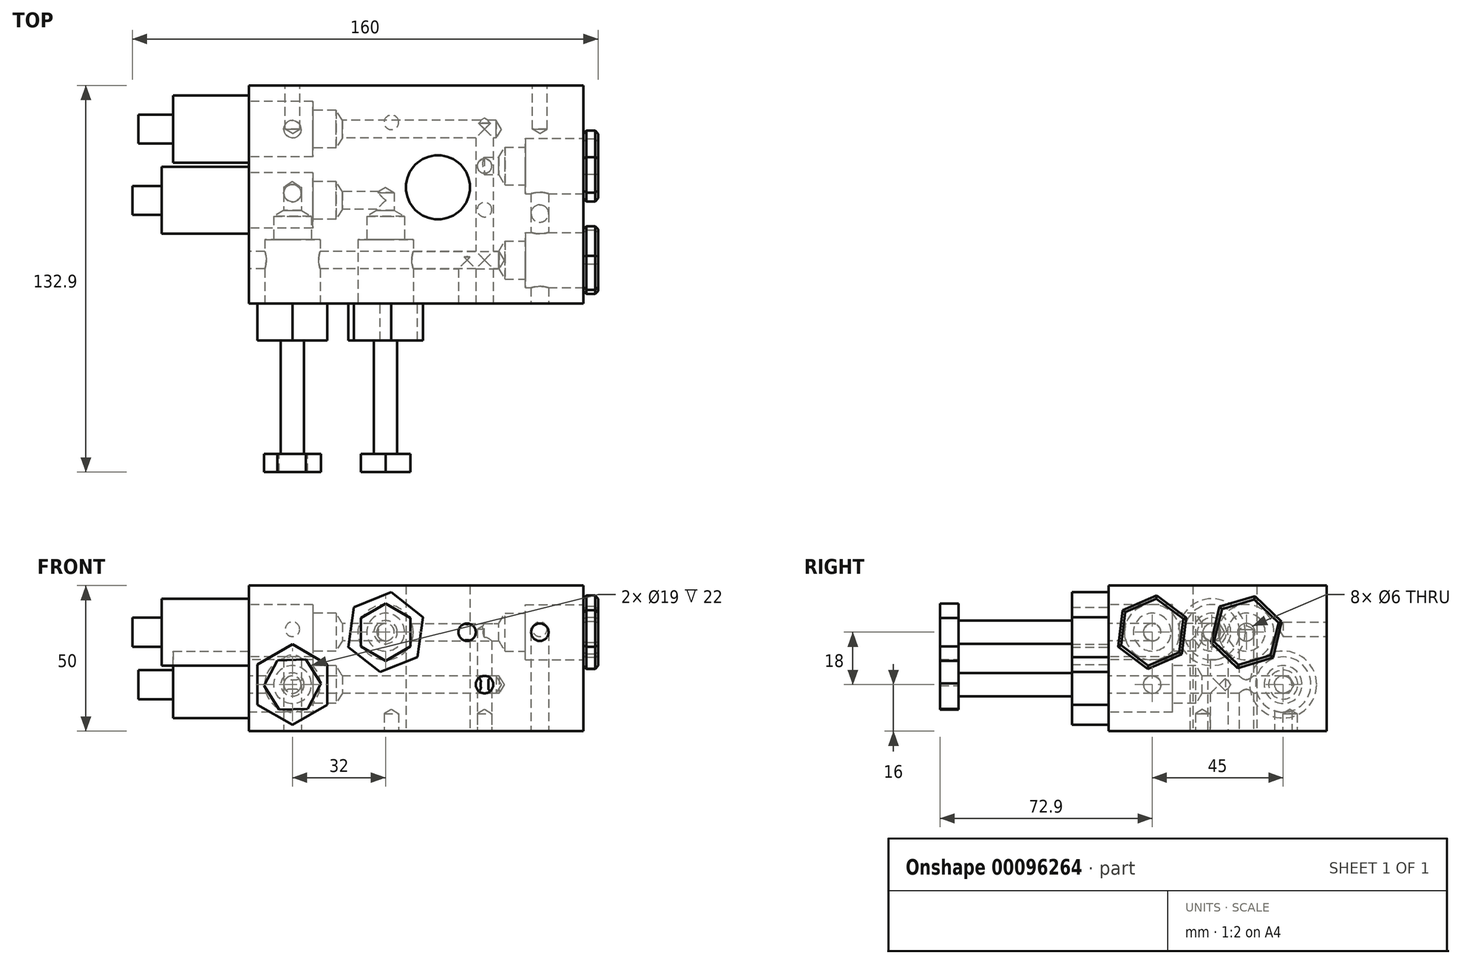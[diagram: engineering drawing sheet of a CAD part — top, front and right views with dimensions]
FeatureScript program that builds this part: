
annotation { "Feature Type Name" : "Feature", "Feature Type Description" : "" }
export const myFeature = defineFeature(function(context is Context, id is Id, definition is map)
    precondition{}
    {
        {
            var Q0;
            Q0=qCreatedBy(makeId("Top.planeOp"),FACE);
            var sketch = newSketch(context, id + "F0", { "sketchPlane" : qUnion([Q0])});
            skLineSegment(sketch, "E0.rect.bottom", {"start": v(50, 35) * mm, "end": v(-65, 35) * mm});
            skLineSegment(sketch, "E0.rect.top", {"start": v(50, -40) * mm, "end": v(-65, -40) * mm});
            skLineSegment(sketch, "E0.rect.left", {"start": v(50, 35) * mm, "end": v(50, -40) * mm});
            skLineSegment(sketch, "E0.rect.right", {"start": v(-65, 35) * mm, "end": v(-65, -40) * mm});
            skPoint(sketch, "E0.rect.middle", {"position": v(0, 0) * mm});
            skSolve(sketch);
        }
        {
            var Q0;
            Q0=makeQuery(id+"F0.imprint","IMPRINT",FACE,{"disambiguationData":[TD([[makeQuery(id+"F0.imprint","IMPRINT",EDGE,{"derivedFrom":sQuery(id+"F0.wireOp",EDGE,"E0.rect.bottom")}),1.0]])]});
            var Q1;
            Q1=makeQuery(id+"F0.imprint","IMPRINT",FACE,{"disambiguationData":[TD([[makeQuery(id+"F0.imprint","IMPRINT",EDGE,{"derivedFrom":sQuery(id+"F0.wireOp",EDGE,"7588558b-6d4b-4371-8287-17bf13519ebf.1.0.0")}),1.0]])]});
            var Q2;
            Q2=makeQuery(id+"F0.imprint","IMPRINT",FACE,{"disambiguationData":[TD([[makeQuery(id+"F0.imprint","IMPRINT",EDGE,{"derivedFrom":sQuery(id+"F0.wireOp",EDGE,"7588558b-6d4b-4371-8287-17bf13519ebf.1.1.0")}),1.0]])]});
            var Q3;
            Q3=makeQuery(id+"F0.imprint","IMPRINT",FACE,{"disambiguationData":[TD([[makeQuery(id+"F0.imprint","IMPRINT",EDGE,{"derivedFrom":sQuery(id+"F0.wireOp",EDGE,"f2f94a69-6f03-48d5-8e05-4ef8c2e551b9")}),1.0]])]});
            var Q4;
            Q4=makeQuery(id+"F0.imprint","IMPRINT",FACE,{"disambiguationData":[TD([[makeQuery(id+"F0.imprint","IMPRINT",EDGE,{"derivedFrom":sQuery(id+"F0.wireOp",EDGE,"7588558b-6d4b-4371-8287-17bf13519ebf.0.1.0")}),1.0]])]});
            extrude(context, id + "F1", {"entities" : qUnion([Q0, Q1, Q2, Q3, Q4]), "depth" : 50 * mm});
        }
        {
            var Q0;
            Q0=makeQuery(id+"F1.opExtrude","CAP_FACE",FACE,{"disambiguationData":[OSD([sQuery(id+"F0.wireOp",EDGE,"E0.rect.bottom"),sQuery(id+"F0.wireOp",EDGE,"E0.rect.top"),sQuery(id+"F0.wireOp",EDGE,"E0.rect.left"),sQuery(id+"F0.wireOp",EDGE,"E0.rect.right"),sQuery(id+"F0.wireOp",EDGE,"fc206ab4-4ad2-4e77-9b30-4fb9f0a5357b")])],"isStart":true});
            var sketch = newSketch(context, id + "F2", { "sketchPlane" : qUnion([Q0])});
            skCircle(sketch, "E1", {"center": v(16, 7.68) * mm, "radius": 2.75 * mm});
            skCircle(sketch, "E2", {"center": v(-16, -22.32) * mm, "radius": 2.75 * mm});
            skCircle(sketch, "E3", {"center": v(16, -7.32) * mm, "radius": 2.5 * mm});
            skPoint(sketch, "E4", {"position": v(-50, 2) * mm});
            skPoint(sketch, "E5", {"position": v(35, 9) * mm});
            skPoint(sketch, "E6", {"position": v(-50, -20) * mm});
            skSolve(sketch);
        }
        {
            var Q0;
            Q0=sQuery(id+"F2.wireOp",VERTEX,"E3.center");
            var Q1;
            Q1=makeQuery(id+"F1.opExtrude","SWEPT_BODY",BODY,{"disambiguationData":[OSD([sQuery(id+"F0.wireOp",EDGE,"E0.rect.bottom"),sQuery(id+"F0.wireOp",EDGE,"E0.rect.top"),sQuery(id+"F0.wireOp",EDGE,"E0.rect.left"),sQuery(id+"F0.wireOp",EDGE,"E0.rect.right"),sQuery(id+"F0.wireOp",EDGE,"fc206ab4-4ad2-4e77-9b30-4fb9f0a5357b")])]});
            hole(context, id + "F3", {"style" : HoleStyle.SIMPLE, "holeDiameter" : 5 * mm, "endStyle" : HoleEndStyle.BLIND, "holeDepth" : 35 * mm, "locations" : qUnion([Q0]), "scope" : qUnion([Q1])});
        }
        {
            var Q0;
            Q0=makeQuery(id+"F1.opExtrude","SWEPT_FACE",FACE,{"disambiguationData":[OSD([sQuery(id+"F0.wireOp",EDGE,"E0.rect.left")])]});
            var sketch = newSketch(context, id + "F4", { "sketchPlane" : qUnion([Q0])});
            skLineSegment(sketch, "E7", {"start": v(-25, 34) * mm, "end": v(7.32, 34) * mm, "construction": true});
            skPoint(sketch, "E8", {"position": v(7.32, 34) * mm});
            skPoint(sketch, "E9", {"position": v(-25, 34) * mm});
            skPoint(sketch, "E10.orphan", {"position": v(35, 34) * mm});
            skCircle(sketch, "E11.cCircle", {"center": v(-25, 34) * mm, "radius": 11 * mm, "construction": true});
            skLineSegment(sketch, "E11.0", {"start": v(-35.19, 41.58) * mm, "end": v(-23.53, 46.62) * mm});
            skLineSegment(sketch, "E11.1", {"start": v(-23.53, 46.62) * mm, "end": v(-13.34, 39.03) * mm});
            skLineSegment(sketch, "E11.2", {"start": v(-13.34, 39.03) * mm, "end": v(-14.81, 26.42) * mm});
            skLineSegment(sketch, "E11.3", {"start": v(-14.81, 26.42) * mm, "end": v(-26.47, 21.38) * mm});
            skLineSegment(sketch, "E11.4", {"start": v(-26.47, 21.38) * mm, "end": v(-36.66, 28.97) * mm});
            skLineSegment(sketch, "E11.5", {"start": v(-36.66, 28.97) * mm, "end": v(-35.19, 41.58) * mm});
            skPoint(sketch, "E11.0.midPoint", {"position": v(-29.36, 44.1) * mm});
            skCircle(sketch, "E12.cCircle", {"center": v(7.32, 34) * mm, "radius": 11 * mm, "construction": true});
            skLineSegment(sketch, "E12.0", {"start": v(-1.88, 42.75) * mm, "end": v(10.3, 46.35) * mm});
            skLineSegment(sketch, "E12.1", {"start": v(10.3, 46.35) * mm, "end": v(19.5, 37.6) * mm});
            skLineSegment(sketch, "E12.2", {"start": v(19.5, 37.6) * mm, "end": v(16.52, 25.25) * mm});
            skLineSegment(sketch, "E12.3", {"start": v(16.52, 25.25) * mm, "end": v(4.34, 21.65) * mm});
            skLineSegment(sketch, "E12.4", {"start": v(4.34, 21.65) * mm, "end": v(-4.86, 30.4) * mm});
            skLineSegment(sketch, "E12.5", {"start": v(-4.86, 30.4) * mm, "end": v(-1.88, 42.75) * mm});
            skPoint(sketch, "E12.0.midPoint", {"position": v(4.2, 44.55) * mm});
            skSolve(sketch);
        }
        {
            var Q0;
            Q0=sQuery(id+"F4.wireOp",VERTEX,"E8");
            var Q1;
            Q1=sQuery(id+"F4.wireOp",VERTEX,"E9");
            var Q2;
            Q2=makeQuery(id+"F1.opExtrude","SWEPT_BODY",BODY,{"disambiguationData":[OSD([sQuery(id+"F0.wireOp",EDGE,"E0.rect.bottom"),sQuery(id+"F0.wireOp",EDGE,"E0.rect.top"),sQuery(id+"F0.wireOp",EDGE,"E0.rect.left"),sQuery(id+"F0.wireOp",EDGE,"E0.rect.right"),sQuery(id+"F0.wireOp",EDGE,"fc206ab4-4ad2-4e77-9b30-4fb9f0a5357b")])]});
            hole(context, id + "F5", {"style" : HoleStyle.C_BORE, "endStyle" : HoleEndStyle.BLIND, "holeDiameter" : 13 * mm, "cBoreDiameter" : 19 * mm, "cBoreDepth" : 20 * mm, "holeDepth" : 27 * mm, "locations" : qUnion([Q0, Q1]), "scope" : qUnion([Q2])});
        }
        {
            var Q0;
            Q0=makeQuery(id+"F1.opExtrude","SWEPT_FACE",FACE,{"disambiguationData":[OSD([sQuery(id+"F0.wireOp",EDGE,"E0.rect.top")])]});
            var sketch = newSketch(context, id + "F6", { "sketchPlane" : qUnion([Q0])});
            skLineSegment(sketch, "E13", {"start": v(-65, 34) * mm, "end": v(50, 34) * mm, "construction": true});
            skLineSegment(sketch, "E14", {"start": v(-65, 16) * mm, "end": v(50, 16) * mm, "construction": true});
            skPoint(sketch, "E15", {"position": v(-50, 16) * mm});
            skPoint(sketch, "E16", {"position": v(-18, 34) * mm});
            skPoint(sketch, "E17", {"position": v(35, 34) * mm});
            skPoint(sketch, "E18", {"position": v(10, 34) * mm});
            skPoint(sketch, "E19", {"position": v(16, 16) * mm});
            skSolve(sketch);
        }
        {
            var Q0;
            Q0=sQuery(id+"F6.wireOp",VERTEX,"E19");
            var Q1;
            Q1=makeQuery(id+"F1.opExtrude","SWEPT_BODY",BODY,{"disambiguationData":[OSD([sQuery(id+"F0.wireOp",EDGE,"E0.rect.bottom"),sQuery(id+"F0.wireOp",EDGE,"E0.rect.top"),sQuery(id+"F0.wireOp",EDGE,"E0.rect.left"),sQuery(id+"F0.wireOp",EDGE,"E0.rect.right"),sQuery(id+"F0.wireOp",EDGE,"fc206ab4-4ad2-4e77-9b30-4fb9f0a5357b")])]});
            hole(context, id + "F7", {"style" : HoleStyle.SIMPLE, "holeDiameter" : 6 * mm, "endStyle" : HoleEndStyle.BLIND, "holeDepth" : 62 * mm, "locations" : qUnion([Q0]), "scope" : qUnion([Q1])});
        }
        {
            var Q0;
            Q0=makeQuery(id+"F1.opExtrude","SWEPT_FACE",FACE,{"disambiguationData":[OSD([sQuery(id+"F0.wireOp",EDGE,"E0.rect.right")])]});
            var sketch = newSketch(context, id + "F8", { "sketchPlane" : qUnion([Q0])});
            skPoint(sketch, "E20", {"position": v(25, 16) * mm});
            skPoint(sketch, "E21", {"position": v(4.5, 34) * mm});
            skPoint(sketch, "E22", {"position": v(-20, 16) * mm});
            skCircle(sketch, "E23", {"center": v(4.5, 34) * mm, "radius": 11.5 * mm});
            skSolve(sketch);
        }
        {
            var Q0;
            Q0=sQuery(id+"F8.wireOp",VERTEX,"E20");
            var Q1;
            Q1=makeQuery(id+"F1.opExtrude","SWEPT_BODY",BODY,{"disambiguationData":[OSD([sQuery(id+"F0.wireOp",EDGE,"E0.rect.bottom"),sQuery(id+"F0.wireOp",EDGE,"E0.rect.top"),sQuery(id+"F0.wireOp",EDGE,"E0.rect.left"),sQuery(id+"F0.wireOp",EDGE,"E0.rect.right"),sQuery(id+"F0.wireOp",EDGE,"fc206ab4-4ad2-4e77-9b30-4fb9f0a5357b")])]});
            hole(context, id + "F9", {"style" : HoleStyle.SIMPLE, "endStyle" : HoleEndStyle.BLIND, "holeDiameter" : 6 * mm, "holeDepth" : 86 * mm, "locations" : qUnion([Q0]), "scope" : qUnion([Q1])});
        }
        {
            var Q0;
            Q0=sQuery(id+"F6.wireOp",VERTEX,"E15");
            var Q1;
            Q1=sQuery(id+"F6.wireOp",VERTEX,"E16");
            var Q2;
            Q2=makeQuery(id+"F1.opExtrude","SWEPT_BODY",BODY,{"disambiguationData":[OSD([sQuery(id+"F0.wireOp",EDGE,"E0.rect.bottom"),sQuery(id+"F0.wireOp",EDGE,"E0.rect.top"),sQuery(id+"F0.wireOp",EDGE,"E0.rect.left"),sQuery(id+"F0.wireOp",EDGE,"E0.rect.right"),sQuery(id+"F0.wireOp",EDGE,"fc206ab4-4ad2-4e77-9b30-4fb9f0a5357b")])]});
            hole(context, id + "F10", {"style" : HoleStyle.C_BORE, "endStyle" : HoleEndStyle.BLIND, "holeDiameter" : 13 * mm, "cBoreDiameter" : 19 * mm, "cBoreDepth" : 22 * mm, "holeDepth" : 30 * mm, "locations" : qUnion([Q0, Q1]), "scope" : qUnion([Q2])});
        }
        {
            var Q0;
            Q0=sQuery(id+"F6.wireOp",VERTEX,"E15");
            var Q1;
            Q1=makeQuery(id+"F1.opExtrude","SWEPT_BODY",BODY,{"disambiguationData":[OSD([sQuery(id+"F0.wireOp",EDGE,"E0.rect.bottom"),sQuery(id+"F0.wireOp",EDGE,"E0.rect.top"),sQuery(id+"F0.wireOp",EDGE,"E0.rect.left"),sQuery(id+"F0.wireOp",EDGE,"E0.rect.right"),sQuery(id+"F0.wireOp",EDGE,"fc206ab4-4ad2-4e77-9b30-4fb9f0a5357b")])]});
            hole(context, id + "F11", {"style" : HoleStyle.SIMPLE, "endStyle" : HoleEndStyle.BLIND, "holeDiameter" : 6 * mm, "holeDepth" : 8 * mm, "locations" : qUnion([Q0]), "scope" : qUnion([Q1])});
        }
        {
            var Q0;
            Q0=sQuery(id+"F4.wireOp",VERTEX,"E8");
            var Q1;
            Q1=makeQuery(id+"F1.opExtrude","SWEPT_BODY",BODY,{"disambiguationData":[OSD([sQuery(id+"F0.wireOp",EDGE,"E0.rect.bottom"),sQuery(id+"F0.wireOp",EDGE,"E0.rect.top"),sQuery(id+"F0.wireOp",EDGE,"E0.rect.left"),sQuery(id+"F0.wireOp",EDGE,"E0.rect.right"),sQuery(id+"F0.wireOp",EDGE,"fc206ab4-4ad2-4e77-9b30-4fb9f0a5357b")])]});
            hole(context, id + "F12", {"style" : HoleStyle.SIMPLE, "endStyle" : HoleEndStyle.BLIND, "holeDiameter" : 6 * mm, "holeDepth" : 5 * mm, "locations" : qUnion([Q0]), "scope" : qUnion([Q1])});
        }
        {
            var Q0;
            Q0=sQuery(id+"F6.wireOp",VERTEX,"E18");
            var Q1;
            Q1=makeQuery(id+"F1.opExtrude","SWEPT_BODY",BODY,{"disambiguationData":[OSD([sQuery(id+"F0.wireOp",EDGE,"E0.rect.bottom"),sQuery(id+"F0.wireOp",EDGE,"E0.rect.top"),sQuery(id+"F0.wireOp",EDGE,"E0.rect.left"),sQuery(id+"F0.wireOp",EDGE,"E0.rect.right"),sQuery(id+"F0.wireOp",EDGE,"fc206ab4-4ad2-4e77-9b30-4fb9f0a5357b")])]});
            hole(context, id + "F13", {"style" : HoleStyle.SIMPLE, "endStyle" : HoleEndStyle.BLIND, "holeDiameter" : 6 * mm, "holeDepth" : 16 * mm, "locations" : qUnion([Q0]), "scope" : qUnion([Q1])});
        }
        {
            var Q0;
            Q0=sQuery(id+"F4.wireOp",VERTEX,"E9");
            var Q1;
            Q1=makeQuery(id+"F1.opExtrude","SWEPT_BODY",BODY,{"disambiguationData":[OSD([sQuery(id+"F0.wireOp",EDGE,"E0.rect.bottom"),sQuery(id+"F0.wireOp",EDGE,"E0.rect.top"),sQuery(id+"F0.wireOp",EDGE,"E0.rect.left"),sQuery(id+"F0.wireOp",EDGE,"E0.rect.right"),sQuery(id+"F0.wireOp",EDGE,"fc206ab4-4ad2-4e77-9b30-4fb9f0a5357b")])]});
            hole(context, id + "F14", {"style" : HoleStyle.SIMPLE, "endStyle" : HoleEndStyle.BLIND, "holeDiameter" : 6 * mm, "holeDepth" : 30 * mm, "locations" : qUnion([Q0]), "scope" : qUnion([Q1])});
        }
        {
            var Q0;
            Q0=sQuery(id+"F6.wireOp",VERTEX,"E17");
            var Q1;
            Q1=makeQuery(id+"F1.opExtrude","SWEPT_BODY",BODY,{"disambiguationData":[OSD([sQuery(id+"F0.wireOp",EDGE,"E0.rect.bottom"),sQuery(id+"F0.wireOp",EDGE,"E0.rect.top"),sQuery(id+"F0.wireOp",EDGE,"E0.rect.left"),sQuery(id+"F0.wireOp",EDGE,"E0.rect.right"),sQuery(id+"F0.wireOp",EDGE,"fc206ab4-4ad2-4e77-9b30-4fb9f0a5357b")])]});
            hole(context, id + "F15", {"style" : HoleStyle.SIMPLE, "endStyle" : HoleEndStyle.BLIND, "holeDiameter" : 6 * mm, "holeDepth" : 50 * mm, "locations" : qUnion([Q0]), "scope" : qUnion([Q1])});
        }
        {
            var Q0;
            Q0=sQuery(id+"F4.wireOp",VERTEX,"53e86b82-a842-4255-912a-a7488f70ac65");
            var Q1;
            Q1=sQuery(id+"F2.wireOp",VERTEX,"E5");
            var Q2;
            Q2=makeQuery(id+"F1.opExtrude","SWEPT_BODY",BODY,{"disambiguationData":[OSD([sQuery(id+"F0.wireOp",EDGE,"E0.rect.bottom"),sQuery(id+"F0.wireOp",EDGE,"E0.rect.top"),sQuery(id+"F0.wireOp",EDGE,"E0.rect.left"),sQuery(id+"F0.wireOp",EDGE,"E0.rect.right"),sQuery(id+"F0.wireOp",EDGE,"fc206ab4-4ad2-4e77-9b30-4fb9f0a5357b")])]});
            hole(context, id + "F16", {"style" : HoleStyle.SIMPLE, "endStyle" : HoleEndStyle.BLIND, "holeDiameter" : 6 * mm, "holeDepth" : 34 * mm, "locations" : qUnion([Q0, Q1]), "scope" : qUnion([Q2])});
        }
        {
            var Q0;
            Q0=sQuery(id+"F8.wireOp",VERTEX,"E21");
            var Q1;
            Q1=makeQuery(id+"F1.opExtrude","SWEPT_BODY",BODY,{"disambiguationData":[OSD([sQuery(id+"F0.wireOp",EDGE,"E0.rect.bottom"),sQuery(id+"F0.wireOp",EDGE,"E0.rect.top"),sQuery(id+"F0.wireOp",EDGE,"E0.rect.left"),sQuery(id+"F0.wireOp",EDGE,"E0.rect.right"),sQuery(id+"F0.wireOp",EDGE,"fc206ab4-4ad2-4e77-9b30-4fb9f0a5357b")])]});
            hole(context, id + "F17", {"style" : HoleStyle.C_BORE, "endStyle" : HoleEndStyle.BLIND, "holeDiameter" : 13 * mm, "cBoreDiameter" : 19 * mm, "cBoreDepth" : 22 * mm, "holeDepth" : 30 * mm, "locations" : qUnion([Q0]), "scope" : qUnion([Q1])});
        }
        {
            var Q0;
            Q0=sQuery(id+"F8.wireOp",VERTEX,"E21");
            var Q1;
            Q1=makeQuery(id+"F1.opExtrude","SWEPT_BODY",BODY,{"disambiguationData":[OSD([sQuery(id+"F0.wireOp",EDGE,"E0.rect.bottom"),sQuery(id+"F0.wireOp",EDGE,"E0.rect.top"),sQuery(id+"F0.wireOp",EDGE,"E0.rect.left"),sQuery(id+"F0.wireOp",EDGE,"E0.rect.right"),sQuery(id+"F0.wireOp",EDGE,"fc206ab4-4ad2-4e77-9b30-4fb9f0a5357b")])]});
            hole(context, id + "F18", {"style" : HoleStyle.SIMPLE, "endStyle" : HoleEndStyle.BLIND, "holeDiameter" : 6 * mm, "holeDepth" : 15 * mm, "locations" : qUnion([Q0]), "scope" : qUnion([Q1])});
        }
        {
            var Q0;
            Q0=sQuery(id+"F2.wireOp",VERTEX,"E4");
            var Q1;
            Q1=makeQuery(id+"F1.opExtrude","SWEPT_BODY",BODY,{"disambiguationData":[OSD([sQuery(id+"F0.wireOp",EDGE,"E0.rect.bottom"),sQuery(id+"F0.wireOp",EDGE,"E0.rect.top"),sQuery(id+"F0.wireOp",EDGE,"E0.rect.left"),sQuery(id+"F0.wireOp",EDGE,"E0.rect.right"),sQuery(id+"F0.wireOp",EDGE,"fc206ab4-4ad2-4e77-9b30-4fb9f0a5357b")])]});
            hole(context, id + "F19", {"style" : HoleStyle.SIMPLE, "endStyle" : HoleEndStyle.BLIND, "holeDiameter" : 6 * mm, "holeDepth" : 35 * mm, "locations" : qUnion([Q0]), "scope" : qUnion([Q1])});
        }
        {
            var Q0;
            Q0=sQuery(id+"F6.wireOp",VERTEX,"E16");
            var Q1;
            Q1=makeQuery(id+"F1.opExtrude","SWEPT_BODY",BODY,{"disambiguationData":[OSD([sQuery(id+"F0.wireOp",EDGE,"E0.rect.bottom"),sQuery(id+"F0.wireOp",EDGE,"E0.rect.top"),sQuery(id+"F0.wireOp",EDGE,"E0.rect.left"),sQuery(id+"F0.wireOp",EDGE,"E0.rect.right"),sQuery(id+"F0.wireOp",EDGE,"fc206ab4-4ad2-4e77-9b30-4fb9f0a5357b")])]});
            hole(context, id + "F20", {"style" : HoleStyle.SIMPLE, "endStyle" : HoleEndStyle.BLIND, "holeDiameter" : 6 * mm, "holeDepth" : 6 * mm, "locations" : qUnion([Q0]), "scope" : qUnion([Q1])});
        }
        {
            var Q0;
            Q0=makeQuery(id+"F1.opExtrude","SWEPT_FACE",FACE,{"disambiguationData":[OSD([sQuery(id+"F0.wireOp",EDGE,"E0.rect.bottom")])]});
            var sketch = newSketch(context, id + "F21", { "sketchPlane" : qUnion([Q0])});
            skPoint(sketch, "E24", {"position": v(-35, 35) * mm});
            skPoint(sketch, "E25.1.0.0", {"position": v(50, 35) * mm});
            skLineSegment(sketch, "E25.direction1", {"start": v(-35, 35) * mm, "end": v(50, 35) * mm, "construction": true});
            skSolve(sketch);
        }
        {
            var Q0;
            Q0=sQuery(id+"F21.wireOp",VERTEX,"E25.1.0.0");
            var Q1;
            Q1=sQuery(id+"F21.wireOp",VERTEX,"E24");
            var Q2;
            Q2=makeQuery(id+"F1.opExtrude","SWEPT_BODY",BODY,{"disambiguationData":[OSD([sQuery(id+"F0.wireOp",EDGE,"E0.rect.bottom"),sQuery(id+"F0.wireOp",EDGE,"E0.rect.top"),sQuery(id+"F0.wireOp",EDGE,"E0.rect.left"),sQuery(id+"F0.wireOp",EDGE,"E0.rect.right"),sQuery(id+"F0.wireOp",EDGE,"fc206ab4-4ad2-4e77-9b30-4fb9f0a5357b")])]});
            hole(context, id + "F22", {"style" : HoleStyle.SIMPLE, "endStyle" : HoleEndStyle.BLIND, "holeDiameter" : 5 * mm, "holeDepth" : 15 * mm, "locations" : qUnion([Q0, Q1]), "scope" : qUnion([Q2])});
        }
        {
            var Q0;
            Q0=sQuery(id+"F0.wireOp",VERTEX,"E0.rect.middle");
            var Q1;
            Q1=makeQuery(id+"F1.opExtrude","SWEPT_BODY",BODY,{"disambiguationData":[OSD([sQuery(id+"F0.wireOp",EDGE,"E0.rect.bottom"),sQuery(id+"F0.wireOp",EDGE,"E0.rect.top"),sQuery(id+"F0.wireOp",EDGE,"E0.rect.left"),sQuery(id+"F0.wireOp",EDGE,"E0.rect.right")])]});
            hole(context, id + "F23", {"style" : HoleStyle.SIMPLE, "endStyle" : HoleEndStyle.THROUGH, "oppositeDirection" : true, "holeDiameter" : 22 * mm, "locations" : qUnion([Q0]), "scope" : qUnion([Q1]), "isTappedThrough" : true});
        }
        {
            var Q0;
            {var subQ0=sQuery(id+"F0.wireOp",EDGE,"E0.rect.right");Q0=makeQuery(id+"F8.imprint","IMPRINT",FACE,{"disambiguationData":[TD([[makeQuery(id+"F8.imprint","IMPRINT",EDGE,{"derivedFrom":makeQuery(id+"F1.opExtrude","CAP_EDGE",EDGE,{"disambiguationData":[OSD([subQ0])],"isStart":true})}),1.0]])]});}
            var sketch = newSketch(context, id + "F24", { "sketchPlane" : qUnion([Q0])});
            skCircle(sketch, "E26", {"center": v(-20, 16) * mm, "radius": 11.5 * mm});
            skSolve(sketch);
        }
        {
            var Q0;
            Q0=makeQuery(id+"F24.imprint","IMPRINT",FACE,{"disambiguationData":[TD([[makeQuery(id+"F24.imprint","IMPRINT",EDGE,{"derivedFrom":sQuery(id+"F24.wireOp",EDGE,"E26")}),1.0]])]});
            extrude(context, id + "F25", {"entities" : qUnion([Q0]), "depth" : 26 * mm});
        }
        {
            var Q0;
            Q0=makeQuery(id+"F25.opExtrude","CAP_FACE",FACE,{"disambiguationData":[OSD([sQuery(id+"F24.wireOp",EDGE,"E26")])],"isStart":false});
            var sketch = newSketch(context, id + "F26", { "sketchPlane" : qUnion([Q0])});
            skCircle(sketch, "E27", {"center": v(-20, 16) * mm, "radius": 5 * mm});
            skSolve(sketch);
        }
        {
            var Q0;
            Q0=sQuery(id+"F8.wireOp",VERTEX,"E22");
            var Q1;
            Q1=makeQuery(id+"F1.opExtrude","SWEPT_BODY",BODY,{"disambiguationData":[OSD([sQuery(id+"F0.wireOp",EDGE,"E0.rect.bottom"),sQuery(id+"F0.wireOp",EDGE,"E0.rect.top"),sQuery(id+"F0.wireOp",EDGE,"E0.rect.left"),sQuery(id+"F0.wireOp",EDGE,"E0.rect.right")])]});
            hole(context, id + "F27", {"style" : HoleStyle.C_BORE, "endStyle" : HoleEndStyle.BLIND, "holeDiameter" : 13 * mm, "cBoreDiameter" : 19 * mm, "cBoreDepth" : 22 * mm, "holeDepth" : 30 * mm, "startFromSketch" : true, "locations" : qUnion([Q0]), "scope" : qUnion([Q1])});
        }
        {
            var Q0;
            Q0=sQuery(id+"F8.wireOp",VERTEX,"E22");
            var Q1;
            Q1=makeQuery(id+"F1.opExtrude","SWEPT_BODY",BODY,{"disambiguationData":[OSD([sQuery(id+"F0.wireOp",EDGE,"E0.rect.bottom"),sQuery(id+"F0.wireOp",EDGE,"E0.rect.top"),sQuery(id+"F0.wireOp",EDGE,"E0.rect.left"),sQuery(id+"F0.wireOp",EDGE,"E0.rect.right")])]});
            hole(context, id + "F28", {"style" : HoleStyle.SIMPLE, "endStyle" : HoleEndStyle.BLIND, "holeDiameter" : 6 * mm, "holeDepth" : 85 * mm, "startFromSketch" : true, "locations" : qUnion([Q0]), "scope" : qUnion([Q1])});
        }
        {
            var Q0;
            Q0=makeQuery(id+"F4.imprint","IMPRINT",FACE,{"disambiguationData":[TD([[makeQuery(id+"F4.imprint","IMPRINT",EDGE,{"derivedFrom":sQuery(id+"F4.wireOp",EDGE,"E11.0")}),-1.0]])]});
            var Q1;
            Q1=makeQuery(id+"F4.imprint","IMPRINT",FACE,{"disambiguationData":[TD([[makeQuery(id+"F4.imprint","IMPRINT",EDGE,{"derivedFrom":sQuery(id+"F4.wireOp",EDGE,"E12.0")}),-1.0]])]});
            extrude(context, id + "F29", {"entities" : qUnion([Q0, Q1]), "depth" : 5 * mm});
        }
        {
            var Q0;
            Q0=makeQuery(id+"F29.opExtrude","CAP_EDGE",EDGE,{"disambiguationData":[OSD([sQuery(id+"F4.wireOp",EDGE,"E11.3")])],"isStart":true});
            var Q1;
            Q1=makeQuery(id+"F29.opExtrude","CAP_EDGE",EDGE,{"disambiguationData":[OSD([sQuery(id+"F4.wireOp",EDGE,"E11.4")])],"isStart":true});
            var Q2;
            Q2=makeQuery(id+"F29.opExtrude","CAP_EDGE",EDGE,{"disambiguationData":[OSD([sQuery(id+"F4.wireOp",EDGE,"E11.5")])],"isStart":true});
            var Q3;
            Q3=makeQuery(id+"F29.opExtrude","CAP_EDGE",EDGE,{"disambiguationData":[OSD([sQuery(id+"F4.wireOp",EDGE,"E11.4")])],"isStart":false});
            var Q4;
            Q4=makeQuery(id+"F29.opExtrude","CAP_EDGE",EDGE,{"disambiguationData":[OSD([sQuery(id+"F4.wireOp",EDGE,"E11.3")])],"isStart":false});
            var Q5;
            Q5=makeQuery(id+"F29.opExtrude","CAP_EDGE",EDGE,{"disambiguationData":[OSD([sQuery(id+"F4.wireOp",EDGE,"E11.2")])],"isStart":false});
            var Q6;
            Q6=makeQuery(id+"F29.opExtrude","CAP_EDGE",EDGE,{"disambiguationData":[OSD([sQuery(id+"F4.wireOp",EDGE,"E11.1")])],"isStart":false});
            var Q7;
            Q7=makeQuery(id+"F29.opExtrude","CAP_EDGE",EDGE,{"disambiguationData":[OSD([sQuery(id+"F4.wireOp",EDGE,"E11.0")])],"isStart":false});
            var Q8;
            Q8=makeQuery(id+"F29.opExtrude","CAP_EDGE",EDGE,{"disambiguationData":[OSD([sQuery(id+"F4.wireOp",EDGE,"E11.5")])],"isStart":false});
            var Q9;
            Q9=makeQuery(id+"F29.opExtrude","CAP_EDGE",EDGE,{"disambiguationData":[OSD([sQuery(id+"F4.wireOp",EDGE,"E11.0")])],"isStart":true});
            var Q10;
            Q10=makeQuery(id+"F29.opExtrude","CAP_EDGE",EDGE,{"disambiguationData":[OSD([sQuery(id+"F4.wireOp",EDGE,"E11.1")])],"isStart":true});
            var Q11;
            Q11=makeQuery(id+"F29.opExtrude","CAP_EDGE",EDGE,{"disambiguationData":[OSD([sQuery(id+"F4.wireOp",EDGE,"E11.2")])],"isStart":true});
            var Q12;
            Q12=makeQuery(id+"F29.opExtrude","CAP_EDGE",EDGE,{"disambiguationData":[OSD([sQuery(id+"F4.wireOp",EDGE,"E12.4")])],"isStart":false});
            var Q13;
            Q13=makeQuery(id+"F29.opExtrude","CAP_EDGE",EDGE,{"disambiguationData":[OSD([sQuery(id+"F4.wireOp",EDGE,"E12.4")])],"isStart":true});
            var Q14;
            Q14=makeQuery(id+"F29.opExtrude","CAP_EDGE",EDGE,{"disambiguationData":[OSD([sQuery(id+"F4.wireOp",EDGE,"E12.3")])],"isStart":false});
            var Q15;
            Q15=makeQuery(id+"F29.opExtrude","CAP_EDGE",EDGE,{"disambiguationData":[OSD([sQuery(id+"F4.wireOp",EDGE,"E12.3")])],"isStart":true});
            var Q16;
            Q16=makeQuery(id+"F29.opExtrude","CAP_EDGE",EDGE,{"disambiguationData":[OSD([sQuery(id+"F4.wireOp",EDGE,"E12.2")])],"isStart":false});
            var Q17;
            Q17=makeQuery(id+"F29.opExtrude","CAP_EDGE",EDGE,{"disambiguationData":[OSD([sQuery(id+"F4.wireOp",EDGE,"E12.2")])],"isStart":true});
            var Q18;
            Q18=makeQuery(id+"F29.opExtrude","CAP_EDGE",EDGE,{"disambiguationData":[OSD([sQuery(id+"F4.wireOp",EDGE,"E12.1")])],"isStart":false});
            var Q19;
            Q19=makeQuery(id+"F29.opExtrude","CAP_EDGE",EDGE,{"disambiguationData":[OSD([sQuery(id+"F4.wireOp",EDGE,"E12.1")])],"isStart":true});
            var Q20;
            Q20=makeQuery(id+"F29.opExtrude","CAP_EDGE",EDGE,{"disambiguationData":[OSD([sQuery(id+"F4.wireOp",EDGE,"E12.5")])],"isStart":false});
            var Q21;
            Q21=makeQuery(id+"F29.opExtrude","CAP_EDGE",EDGE,{"disambiguationData":[OSD([sQuery(id+"F4.wireOp",EDGE,"E12.5")])],"isStart":true});
            var Q22;
            Q22=makeQuery(id+"F29.opExtrude","CAP_EDGE",EDGE,{"disambiguationData":[OSD([sQuery(id+"F4.wireOp",EDGE,"E12.0")])],"isStart":true});
            var Q23;
            Q23=makeQuery(id+"F29.opExtrude","CAP_EDGE",EDGE,{"disambiguationData":[OSD([sQuery(id+"F4.wireOp",EDGE,"E12.0")])],"isStart":false});
            chamfer(context, id + "F30", {"entities" : qUnion([Q0, Q1, Q2, Q3, Q4, Q5, Q6, Q7, Q8, Q9, Q10, Q11, Q12, Q13, Q14, Q15, Q16, Q17, Q18, Q19, Q20, Q21, Q22, Q23]), "width" : 1 * mm, "tangentPropagation" : true});
        }
        {
            var Q0;
            Q0=makeQuery(id+"F26.imprint","IMPRINT",FACE,{"disambiguationData":[TD([[makeQuery(id+"F26.imprint","IMPRINT",EDGE,{"derivedFrom":sQuery(id+"F26.wireOp",EDGE,"E27")}),1.0]])]});
            extrude(context, id + "F31", {"entities" : qUnion([Q0]), "operationType" : NewBodyOperationType.ADD, "depth" : 12 * mm});
        }
        {
            var Q0;
            Q0=makeQuery(id+"F8.imprint","IMPRINT",FACE,{"disambiguationData":[TD([[makeQuery(id+"F8.imprint","IMPRINT",EDGE,{"derivedFrom":sQuery(id+"F8.wireOp",EDGE,"E23")}),1.0]])]});
            extrude(context, id + "F32", {"entities" : qUnion([Q0]), "depth" : 30 * mm});
        }
        {
            var Q0;
            Q0=makeQuery(id+"F32.opExtrude","CAP_FACE",FACE,{"disambiguationData":[OSD([sQuery(id+"F8.wireOp",EDGE,"E23")])],"isStart":false});
            var sketch = newSketch(context, id + "F33", { "sketchPlane" : qUnion([Q0])});
            skCircle(sketch, "E28", {"center": v(4.5, 34) * mm, "radius": 5 * mm});
            skSolve(sketch);
        }
        {
            var Q0;
            Q0=makeQuery(id+"F33.imprint","IMPRINT",FACE,{"disambiguationData":[TD([[makeQuery(id+"F33.imprint","IMPRINT",EDGE,{"derivedFrom":sQuery(id+"F33.wireOp",EDGE,"E28")}),1.0]])]});
            extrude(context, id + "F34", {"entities" : qUnion([Q0]), "operationType" : NewBodyOperationType.ADD, "depth" : 10 * mm});
        }
        {
            var Q0;
            Q0=sQuery(id+"F2.wireOp",VERTEX,"E6");
            var Q1;
            Q1=makeQuery(id+"F1.opExtrude","SWEPT_BODY",BODY,{"disambiguationData":[OSD([sQuery(id+"F0.wireOp",EDGE,"E0.rect.bottom"),sQuery(id+"F0.wireOp",EDGE,"E0.rect.top"),sQuery(id+"F0.wireOp",EDGE,"E0.rect.left"),sQuery(id+"F0.wireOp",EDGE,"E0.rect.right")])]});
            hole(context, id + "F35", {"style" : HoleStyle.SIMPLE, "endStyle" : HoleEndStyle.BLIND, "holeDiameter" : 6 * mm, "holeDepth" : 18 * mm, "locations" : qUnion([Q0]), "scope" : qUnion([Q1])});
        }
        {
            var Q0;
            {var subQ0=sQuery(id+"F0.wireOp",EDGE,"E0.rect.top");Q0=makeQuery(id+"F6.imprint","IMPRINT",FACE,{"disambiguationData":[TD([[makeQuery(id+"F6.imprint","IMPRINT",EDGE,{"derivedFrom":makeQuery(id+"F1.opExtrude","CAP_EDGE",EDGE,{"disambiguationData":[OSD([subQ0])],"isStart":true})}),-1.0]])]});}
            var sketch = newSketch(context, id + "F36", { "sketchPlane" : qUnion([Q0])});
            skCircle(sketch, "E29.cCircle", {"center": v(-50, 16) * mm, "radius": 12 * mm, "construction": true});
            skLineSegment(sketch, "E29.0", {"start": v(-38, 22.93) * mm, "end": v(-38, 9.07) * mm});
            skLineSegment(sketch, "E29.1", {"start": v(-38, 9.07) * mm, "end": v(-50, 2.14) * mm});
            skLineSegment(sketch, "E29.2", {"start": v(-50, 2.14) * mm, "end": v(-62, 9.07) * mm});
            skLineSegment(sketch, "E29.3", {"start": v(-62, 9.07) * mm, "end": v(-62, 22.93) * mm});
            skLineSegment(sketch, "E29.4", {"start": v(-62, 22.93) * mm, "end": v(-50, 29.86) * mm});
            skLineSegment(sketch, "E29.5", {"start": v(-50, 29.86) * mm, "end": v(-38, 22.93) * mm});
            skPoint(sketch, "E29.0.midPoint", {"position": v(-38, 16) * mm});
            skCircle(sketch, "E30.cCircle", {"center": v(-18, 34) * mm, "radius": 12 * mm, "construction": true});
            skLineSegment(sketch, "E30.0", {"start": v(-5.15, 39.18) * mm, "end": v(-7.1, 25.46) * mm});
            skLineSegment(sketch, "E30.1", {"start": v(-7.1, 25.46) * mm, "end": v(-19.94, 20.28) * mm});
            skLineSegment(sketch, "E30.2", {"start": v(-19.94, 20.28) * mm, "end": v(-30.85, 28.82) * mm});
            skLineSegment(sketch, "E30.3", {"start": v(-30.85, 28.82) * mm, "end": v(-28.9, 42.54) * mm});
            skLineSegment(sketch, "E30.4", {"start": v(-28.9, 42.54) * mm, "end": v(-16.06, 47.72) * mm});
            skLineSegment(sketch, "E30.5", {"start": v(-16.06, 47.72) * mm, "end": v(-5.15, 39.18) * mm});
            skPoint(sketch, "E30.0.midPoint", {"position": v(-6.12, 32.32) * mm});
            skSolve(sketch);
        }
        {
            var Q0;
            Q0=qSketchRegion(id+"F36",true);
            extrude(context, id + "F37", {"entities" : qUnion([Q0]), "depth" : 12.6 * mm});
        }
        {
            var Q0;
            Q0=makeQuery(id+"F37.opExtrude","CAP_FACE",FACE,{"disambiguationData":[OSD([sQuery(id+"F36.wireOp",EDGE,"E29.0"),sQuery(id+"F36.wireOp",EDGE,"E29.1"),sQuery(id+"F36.wireOp",EDGE,"E29.2"),sQuery(id+"F36.wireOp",EDGE,"E29.3"),sQuery(id+"F36.wireOp",EDGE,"E29.4"),sQuery(id+"F36.wireOp",EDGE,"E29.5")])],"isStart":false});
            var sketch = newSketch(context, id + "F38", { "sketchPlane" : qUnion([Q0])});
            skCircle(sketch, "E31", {"center": v(-50, 16) * mm, "radius": 4 * mm});
            skPoint(sketch, "E31.centerSnap0", {"position": v(-62, 16) * mm});
            skSolve(sketch);
        }
        {
            var Q0;
            Q0=makeQuery(id+"F38.imprint","IMPRINT",FACE,{"disambiguationData":[TD([[makeQuery(id+"F38.imprint","IMPRINT",EDGE,{"derivedFrom":sQuery(id+"F38.wireOp",EDGE,"E31")}),1.0]])]});
            extrude(context, id + "F39", {"entities" : qUnion([Q0]), "operationType" : NewBodyOperationType.ADD, "depth" : 39 * mm});
        }
        {
            var Q0;
            Q0=makeQuery(id+"F39.opExtrude","CAP_FACE",FACE,{"disambiguationData":[OSD([sQuery(id+"F38.wireOp",EDGE,"E31")])],"isStart":false});
            var sketch = newSketch(context, id + "F40", { "sketchPlane" : qUnion([Q0])});
            skCircle(sketch, "E32.cCircle", {"center": v(-50, 16) * mm, "radius": 8.5 * mm, "construction": true});
            skLineSegment(sketch, "E32.0", {"start": v(-45.41, 24.68) * mm, "end": v(-40.2, 16.37) * mm});
            skLineSegment(sketch, "E32.1", {"start": v(-40.2, 16.37) * mm, "end": v(-44.78, 7.69) * mm});
            skLineSegment(sketch, "E32.2", {"start": v(-44.78, 7.69) * mm, "end": v(-54.59, 7.32) * mm});
            skLineSegment(sketch, "E32.3", {"start": v(-54.59, 7.32) * mm, "end": v(-59.8, 15.63) * mm});
            skLineSegment(sketch, "E32.4", {"start": v(-59.8, 15.63) * mm, "end": v(-55.22, 24.31) * mm});
            skLineSegment(sketch, "E32.5", {"start": v(-55.22, 24.31) * mm, "end": v(-45.41, 24.68) * mm});
            skPoint(sketch, "E32.0.midPoint", {"position": v(-42.8, 20.52) * mm});
            skSolve(sketch);
        }
        {
            var Q0;
            Q0=makeQuery(id+"F40.imprint","IMPRINT",FACE,{"disambiguationData":[TD([[makeQuery(id+"F40.imprint","IMPRINT",EDGE,{"derivedFrom":sQuery(id+"F40.wireOp",EDGE,"E32.0")}),-1.0]])]});
            var Q1;
            Q1=makeQuery(id+"F40.imprint","IMPRINT",FACE,{"disambiguationData":[TD([[makeQuery(id+"F40.imprint","IMPRINT",EDGE,{"derivedFrom":makeQuery(id+"F39.opExtrude","CAP_EDGE",EDGE,{"disambiguationData":[OSD([sQuery(id+"F38.wireOp",EDGE,"E31")])],"isStart":false})}),1.0]])]});
            extrude(context, id + "F41", {"entities" : qUnion([Q0, Q1]), "operationType" : NewBodyOperationType.ADD, "depth" : 6.3 * mm});
        }
        {
            var Q0;
            Q0=makeQuery(id+"F37.opExtrude","CAP_FACE",FACE,{"disambiguationData":[OSD([sQuery(id+"F36.wireOp",EDGE,"E30.0"),sQuery(id+"F36.wireOp",EDGE,"E30.1"),sQuery(id+"F36.wireOp",EDGE,"E30.2"),sQuery(id+"F36.wireOp",EDGE,"E30.3"),sQuery(id+"F36.wireOp",EDGE,"E30.4"),sQuery(id+"F36.wireOp",EDGE,"E30.5")])],"isStart":false});
            var sketch = newSketch(context, id + "F42", { "sketchPlane" : qUnion([Q0])});
            skLineSegment(sketch, "E33", {"start": v(-13.52, 22.87) * mm, "end": v(-22.48, 45.13) * mm, "construction": true});
            skCircle(sketch, "E34", {"center": v(-18, 34) * mm, "radius": 4 * mm});
            skSolve(sketch);
        }
        {
            var Q0;
            Q0=makeQuery(id+"F42.imprint","IMPRINT",FACE,{"disambiguationData":[TD([[makeQuery(id+"F42.imprint","IMPRINT",EDGE,{"derivedFrom":sQuery(id+"F42.wireOp",EDGE,"E34")}),1.0]])]});
            extrude(context, id + "F43", {"entities" : qUnion([Q0]), "operationType" : NewBodyOperationType.ADD, "depth" : 39 * mm});
        }
        {
            var Q0;
            Q0=makeQuery(id+"F43.opExtrude","CAP_FACE",FACE,{"disambiguationData":[OSD([sQuery(id+"F42.wireOp",EDGE,"E34")])],"isStart":false});
            var sketch = newSketch(context, id + "F44", { "sketchPlane" : qUnion([Q0])});
            skCircle(sketch, "E35.cCircle", {"center": v(-18, 34) * mm, "radius": 8.5 * mm, "construction": true});
            skLineSegment(sketch, "E35.0", {"start": v(-9.5, 38.9) * mm, "end": v(-9.5, 29.1) * mm});
            skLineSegment(sketch, "E35.1", {"start": v(-9.5, 29.1) * mm, "end": v(-18, 24.19) * mm});
            skLineSegment(sketch, "E35.2", {"start": v(-18, 24.19) * mm, "end": v(-26.5, 29.1) * mm});
            skLineSegment(sketch, "E35.3", {"start": v(-26.5, 29.1) * mm, "end": v(-26.5, 38.9) * mm});
            skLineSegment(sketch, "E35.4", {"start": v(-26.5, 38.9) * mm, "end": v(-18, 43.81) * mm});
            skLineSegment(sketch, "E35.5", {"start": v(-18, 43.81) * mm, "end": v(-9.5, 38.9) * mm});
            skPoint(sketch, "E35.0.midPoint", {"position": v(-9.5, 34) * mm});
            skSolve(sketch);
        }
        {
            var Q0;
            Q0=makeQuery(id+"F44.imprint","IMPRINT",FACE,{"disambiguationData":[TD([[makeQuery(id+"F44.imprint","IMPRINT",EDGE,{"derivedFrom":sQuery(id+"F44.wireOp",EDGE,"E35.0")}),-1.0]])]});
            var Q1;
            Q1=makeQuery(id+"F44.imprint","IMPRINT",FACE,{"disambiguationData":[TD([[makeQuery(id+"F44.imprint","IMPRINT",EDGE,{"derivedFrom":makeQuery(id+"F43.opExtrude","CAP_EDGE",EDGE,{"disambiguationData":[OSD([sQuery(id+"F42.wireOp",EDGE,"E34")])],"isStart":false})}),1.0]])]});
            extrude(context, id + "F45", {"entities" : qUnion([Q0, Q1]), "operationType" : NewBodyOperationType.ADD, "depth" : 6.3 * mm});
        }
        {
            var Q0;
            Q0=sQuery(id+"F2.wireOp",VERTEX,"E2.center");
            var Q1;
            Q1=sQuery(id+"F2.wireOp",VERTEX,"E1.center");
            var Q2;
            Q2=makeQuery(id+"F1.opExtrude","SWEPT_BODY",BODY,{"disambiguationData":[OSD([sQuery(id+"F0.wireOp",EDGE,"E0.rect.bottom"),sQuery(id+"F0.wireOp",EDGE,"E0.rect.top"),sQuery(id+"F0.wireOp",EDGE,"E0.rect.left"),sQuery(id+"F0.wireOp",EDGE,"E0.rect.right")])]});
            hole(context, id + "F46", {"style" : HoleStyle.SIMPLE, "endStyle" : HoleEndStyle.BLIND, "holeDiameter" : 5 * mm, "holeDepth" : 6 * mm, "locations" : qUnion([Q0, Q1]), "scope" : qUnion([Q2])});
        }
    });
